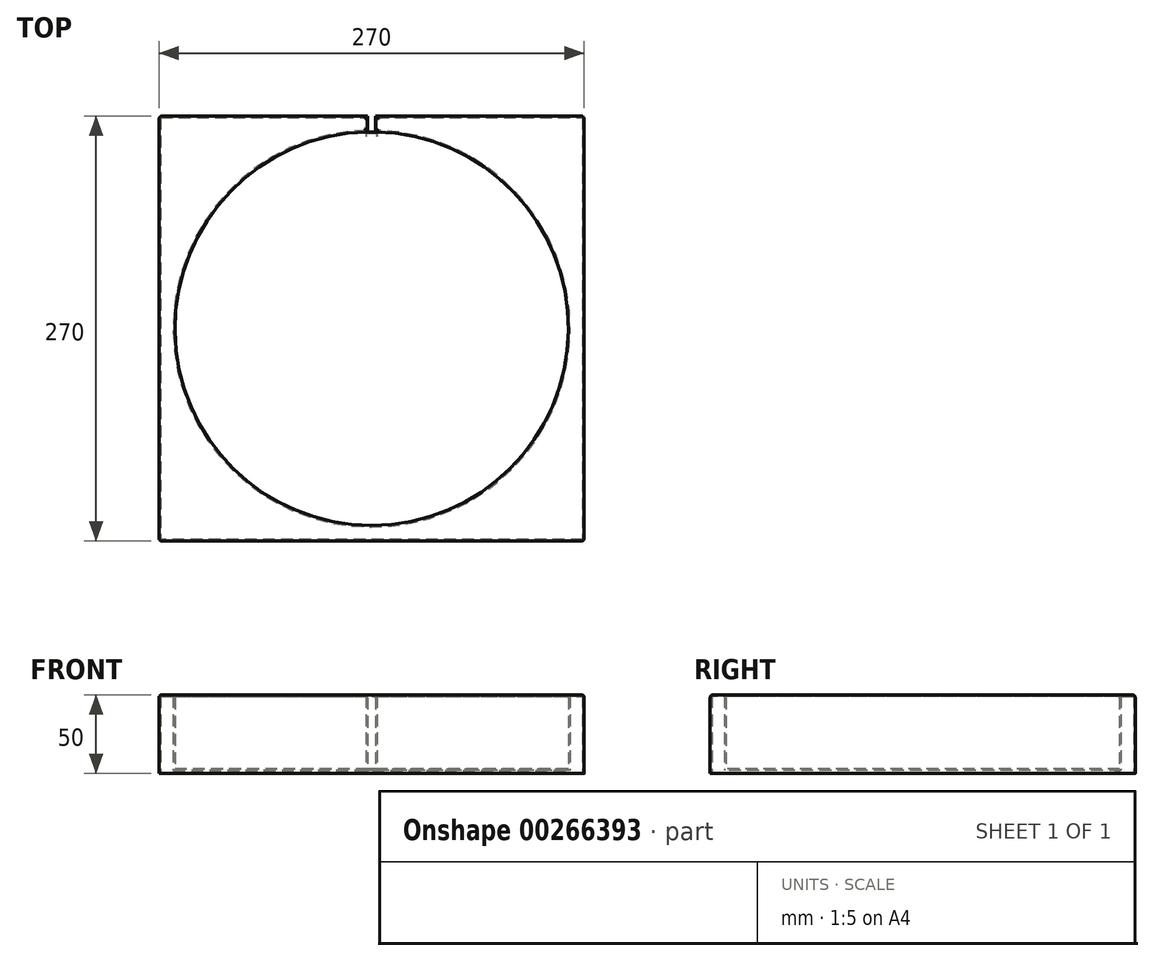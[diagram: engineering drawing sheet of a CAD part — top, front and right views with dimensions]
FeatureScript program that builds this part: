
annotation { "Feature Type Name" : "Feature", "Feature Type Description" : "" }
export const myFeature = defineFeature(function(context is Context, id is Id, definition is map)
    precondition{}
    {
        {
            var Q0;
            Q0=qCreatedBy(makeId("Top.planeOp"),FACE);
            var sketch = newSketch(context, id + "F0", { "sketchPlane" : qUnion([Q0])});
            skLineSegment(sketch, "E0", {"start": v(-135, 135) * mm, "end": v(135, 135) * mm});
            skLineSegment(sketch, "E1", {"start": v(135, 135) * mm, "end": v(135, -135) * mm});
            skLineSegment(sketch, "E2", {"start": v(135, -135) * mm, "end": v(-135, -135) * mm});
            skLineSegment(sketch, "E3", {"start": v(-135, 135) * mm, "end": v(-135, -135) * mm});
            skCircle(sketch, "E4", {"center": v(0, 0) * mm, "radius": 125 * mm});
            skLineSegment(sketch, "E5", {"start": v(-2.5, 135) * mm, "end": v(-2.5, 115) * mm});
            skLineSegment(sketch, "E6", {"start": v(-2.5, 115) * mm, "end": v(2.5, 115) * mm});
            skLineSegment(sketch, "E7", {"start": v(2.5, 115) * mm, "end": v(2.5, 135) * mm});
            skSolve(sketch);
        }
        {
            var Q0;
            Q0=makeQuery(id+"F0.imprint","IMPRINT",FACE,{"disambiguationData":[TD([[makeQuery(id+"F0.imprint","IMPRINT",EDGE,{"derivedFrom":sQuery(id+"F0.wireOp",EDGE,"E0")}),-1.0]])]});
            extrude(context, id + "F1", {"entities" : qUnion([Q0]), "depth" : 50 * mm, "offsetDistance" : 25 * mm});
        }
        {
            var Q0;
            Q0=makeQuery(id+"F0.imprint","IMPRINT",FACE,{"disambiguationData":[TD([[makeQuery(id+"F0.imprint","IMPRINT",EDGE,{"derivedFrom":sQuery(id+"F0.wireOp",EDGE,"E4")}),1.0]])]});
            extrude(context, id + "F2", {"entities" : qUnion([Q0]), "operationType" : NewBodyOperationType.ADD, "depth" : 3 * mm, "offsetDistance" : 25 * mm});
        }
        {
            var Q0;
            {var subQ0=sQuery(id+"F0.wireOp",EDGE,"E4");Q0=makeQuery(id+"F2.boolean.opBoolean","MERGE",FACE,{"derivedFrom":[makeQuery(id+"F1.opExtrude","CAP_FACE",FACE,{"disambiguationData":[OSD([sQuery(id+"F0.wireOp",EDGE,"E0"),sQuery(id+"F0.wireOp",EDGE,"E1"),sQuery(id+"F0.wireOp",EDGE,"E2"),sQuery(id+"F0.wireOp",EDGE,"E3"),subQ0])],"isStart":true}),makeQuery(id+"F2.opExtrude","CAP_FACE",FACE,{"disambiguationData":[OSD([subQ0])],"isStart":true})]});}
            shell(context, id + "F3", {"entities" : qUnion([Q0]), "thickness" : 1 * mm});
        }
        {
            var Q0;
            {var subQ0=sQuery(id+"F0.wireOp",EDGE,"E4");Q0=makeQuery(id+"F3.opShell","OFFSET_EDGE",EDGE,{"disambiguationData":[OSD([subQ0]),TDD([makeQuery(id+"F2.boolean.opBoolean","SPLIT",EDGE,{"disambiguationData":[topologyDisambiguationEdgeConnected([makeQuery(id+"F1.opExtrude","SWEPT_FACE",FACE,{"disambiguationData":[OSD([subQ0])]})])],"derivedFrom":makeQuery(id+"F2.opExtrude","CAP_EDGE",EDGE,{"disambiguationData":[OSD([subQ0])],"isStart":false})})])]});}
            var Q1;
            {var subQ0=sQuery(id+"F0.wireOp",EDGE,"E0");Q1=makeQuery(id+"F1.opExtrude","CAP_EDGE",EDGE,{"disambiguationData":[OSD([subQ0]),TDD([makeQuery(id+"F0.imprint","IMPRINT",EDGE,{"disambiguationData":[TD([[makeQuery(id+"F0.imprint","INTERSECT",VERTEX,{"derivedFrom":[subQ0,sQuery(id+"F0.wireOp",EDGE,"E1")]}),1.0]])],"derivedFrom":subQ0})])],"isStart":false});}
            var Q2;
            {var subQ0=sQuery(id+"F0.wireOp",EDGE,"E0");Q2=makeQuery(id+"F1.opExtrude","CAP_EDGE",EDGE,{"disambiguationData":[OSD([subQ0]),TDD([makeQuery(id+"F0.imprint","IMPRINT",EDGE,{"disambiguationData":[TD([[makeQuery(id+"F0.imprint","INTERSECT",VERTEX,{"derivedFrom":[subQ0,sQuery(id+"F0.wireOp",EDGE,"E3")]}),-1.0]])],"derivedFrom":subQ0})])],"isStart":false});}
            var Q3;
            Q3=makeQuery(id+"F1.opExtrude","SWEPT_EDGE",EDGE,{"disambiguationData":[OSD([sQuery(id+"F0.wireOp",EDGE,"E0"),sQuery(id+"F0.wireOp",EDGE,"E3")])]});
            var Q4;
            Q4=makeQuery(id+"F1.opExtrude","SWEPT_EDGE",EDGE,{"disambiguationData":[OSD([sQuery(id+"F0.wireOp",EDGE,"E0"),sQuery(id+"F0.wireOp",EDGE,"E1")])]});
            var Q5;
            Q5=makeQuery(id+"F1.opExtrude","CAP_EDGE",EDGE,{"disambiguationData":[OSD([sQuery(id+"F0.wireOp",EDGE,"E1")])],"isStart":false});
            var Q6;
            Q6=makeQuery(id+"F1.opExtrude","SWEPT_EDGE",EDGE,{"disambiguationData":[OSD([sQuery(id+"F0.wireOp",EDGE,"E1"),sQuery(id+"F0.wireOp",EDGE,"E2")])]});
            var Q7;
            Q7=makeQuery(id+"F1.opExtrude","CAP_EDGE",EDGE,{"disambiguationData":[OSD([sQuery(id+"F0.wireOp",EDGE,"E2")])],"isStart":false});
            var Q8;
            Q8=makeQuery(id+"F1.opExtrude","SWEPT_EDGE",EDGE,{"disambiguationData":[OSD([sQuery(id+"F0.wireOp",EDGE,"E2"),sQuery(id+"F0.wireOp",EDGE,"E3")])]});
            var Q9;
            Q9=makeQuery(id+"F1.opExtrude","CAP_EDGE",EDGE,{"disambiguationData":[OSD([sQuery(id+"F0.wireOp",EDGE,"E3")])],"isStart":false});
            var Q10;
            Q10=makeQuery(id+"F1.opExtrude","CAP_EDGE",EDGE,{"disambiguationData":[OSD([sQuery(id+"F0.wireOp",EDGE,"E4")])],"isStart":false});
            var Q11;
            Q11=makeQuery(id+"F1.opExtrude","CAP_EDGE",EDGE,{"disambiguationData":[OSD([sQuery(id+"F0.wireOp",EDGE,"E5")])],"isStart":false});
            var Q12;
            Q12=makeQuery(id+"F1.opExtrude","CAP_EDGE",EDGE,{"disambiguationData":[OSD([sQuery(id+"F0.wireOp",EDGE,"E7")])],"isStart":false});
            fillet(context, id + "F4", {"entities" : qUnion([Q0, Q1, Q2, Q3, Q4, Q5, Q6, Q7, Q8, Q9, Q10, Q11, Q12]), "radius" : 2 * mm, "tangentPropagation" : true, "allowEdgeOverflow" : false});
        }
    });
